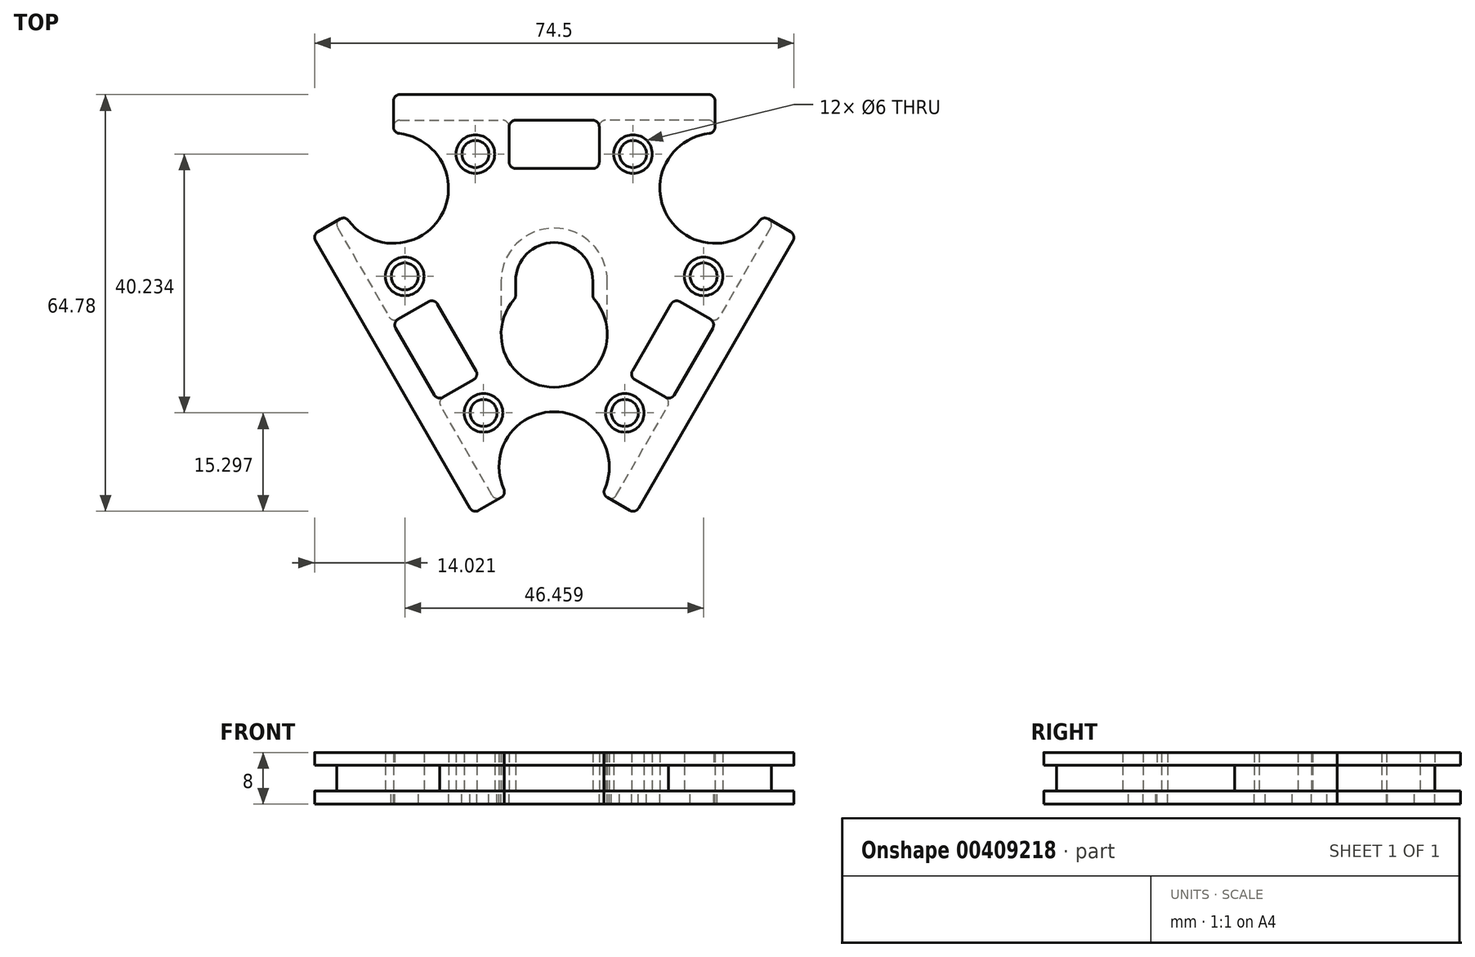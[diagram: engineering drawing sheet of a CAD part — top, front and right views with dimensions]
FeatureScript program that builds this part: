
annotation { "Feature Type Name" : "Feature", "Feature Type Description" : "" }
export const myFeature = defineFeature(function(context is Context, id is Id, definition is map)
    precondition{}
    {
        {
            var Q0;
            Q0=qCreatedBy(makeId("Top.planeOp"),FACE);
            var sketch = newSketch(context, id + "F0", { "sketchPlane" : qUnion([Q0])});
            skLineSegment(sketch, "E0.MirrorCS", {"start": v(-24, 25) * mm, "end": v(-8, 25) * mm});
            skLineSegment(sketch, "E1.MirrorCS", {"start": v(-25, 24) * mm, "end": v(-25, 23.95) * mm});
            skLineSegment(sketch, "E2.1.19", {"start": v(0, 0) * mm, "end": v(-17.58, 10.15) * mm, "construction": true});
            skArc(sketch, "E3", {"start": v(-17.58, 10.15) * mm, "mid": v(-17.37, 18.32) * mm, "end": v(-24.1, 22.95) * mm});
            skLineSegment(sketch, "E4", {"start": v(-25, 23) * mm, "end": v(0, 23) * mm, "construction": true});
            skLineSegment(sketch, "E5.top", {"start": v(0, 17.5) * mm, "end": v(-6, 17.5) * mm});
            skLineSegment(sketch, "E5.right", {"start": v(-7, 24) * mm, "end": v(-7, 18.5) * mm});
            skArc(sketch, "E6", {"start": v(6, 0) * mm, "mid": v(0, 6) * mm, "end": v(-6, 0) * mm});
            skArc(sketch, "E7", {"start": v(-6.24, -2.86) * mm, "mid": v(0, -16.5) * mm, "end": v(6.24, -2.86) * mm});
            skLineSegment(sketch, "E8", {"start": v(0, 27) * mm, "end": v(-25, 27) * mm, "construction": true});
            skCircle(sketch, "E9", {"center": v(-25, 27) * mm, "radius": 2 * mm, "construction": true});
            skLineSegment(sketch, "E10", {"start": v(-17.58, 10.15) * mm, "end": v(-7.85, 27) * mm, "construction": true});
            skLineSegment(sketch, "E11", {"start": v(-6, 0) * mm, "end": v(-6, -2.2) * mm});
            skLineSegment(sketch, "E12", {"start": v(6, -2.2) * mm, "end": v(6, 0) * mm});
            skCircle(sketch, "E13", {"center": v(-12.25, 19.75) * mm, "radius": 3 * mm});
            skCircle(sketch, "E14", {"center": v(-12.25, 19.75) * mm, "radius": 5.25 * mm, "construction": true});
            skPoint(sketch, "E15.visualSharp", {"position": v(-7, 25) * mm});
            skArc(sketch, "E15.filletArc", {"start": v(-7, 24) * mm, "mid": v(-7.3, 24.7) * mm, "end": v(-8, 25) * mm});
            skPoint(sketch, "E16.visualSharp", {"position": v(-25, 25) * mm});
            skArc(sketch, "E16.filletArc", {"start": v(-24, 25) * mm, "mid": v(-24.7, 24.7) * mm, "end": v(-25, 24) * mm});
            skPoint(sketch, "E17.visualSharp", {"position": v(-25, 23) * mm});
            skArc(sketch, "E17.filletArc", {"start": v(-25, 23.95) * mm, "mid": v(-24.74, 23.28) * mm, "end": v(-24.1, 22.95) * mm});
            skPoint(sketch, "E18.visualSharp", {"position": v(-7, 17.5) * mm});
            skArc(sketch, "E18.filletArc", {"start": v(-7, 18.5) * mm, "mid": v(-6.7, 17.8) * mm, "end": v(-6, 17.5) * mm});
            skPoint(sketch, "E19.visualSharp", {"position": v(-6, -2.59) * mm});
            skArc(sketch, "E19.filletArc", {"start": v(-6.24, -2.86) * mm, "mid": v(-6.06, -2.55) * mm, "end": v(-6, -2.2) * mm});
            skPoint(sketch, "E20.visualSharp", {"position": v(6, -2.59) * mm});
            skArc(sketch, "E20.filletArc", {"start": v(6, -2.2) * mm, "mid": v(6.06, -2.55) * mm, "end": v(6.24, -2.86) * mm});
            skLineSegment(sketch, "E21", {"start": v(0, 27) * mm, "end": v(0, 0) * mm, "construction": true});
            skLineSegment(sketch, "E22.MirrorCS", {"start": v(25, 24) * mm, "end": v(25, 23.95) * mm});
            skArc(sketch, "E23.MirrorCS", {"start": v(7, 24) * mm, "mid": v(7.3, 24.7) * mm, "end": v(8, 25) * mm});
            skArc(sketch, "E24.MirrorCS", {"start": v(24, 25) * mm, "mid": v(24.7, 24.7) * mm, "end": v(25, 24) * mm});
            skArc(sketch, "E25.MirrorCS", {"start": v(25, 23.95) * mm, "mid": v(24.74, 23.28) * mm, "end": v(24.1, 22.95) * mm});
            skArc(sketch, "E26.MirrorCS", {"start": v(7, 18.5) * mm, "mid": v(6.7, 17.8) * mm, "end": v(6, 17.5) * mm});
            skLineSegment(sketch, "E27.MirrorCS", {"start": v(25, 23) * mm, "end": v(0, 23) * mm, "construction": true});
            skLineSegment(sketch, "E28.MirrorCS", {"start": v(7, 24) * mm, "end": v(7, 18.5) * mm});
            skArc(sketch, "E29.MirrorCS", {"start": v(17.58, 10.15) * mm, "mid": v(17.37, 18.32) * mm, "end": v(24.1, 22.95) * mm});
            skPoint(sketch, "E30.MirrorP", {"position": v(25, 23) * mm});
            skPoint(sketch, "E31.MirrorP", {"position": v(25, 25) * mm});
            skPoint(sketch, "E32.MirrorP", {"position": v(7, 17.5) * mm});
            skCircle(sketch, "E33.MirrorC", {"center": v(12.25, 19.75) * mm, "radius": 5.25 * mm, "construction": true});
            skLineSegment(sketch, "E34.MirrorCS", {"start": v(24, 25) * mm, "end": v(8, 25) * mm});
            skLineSegment(sketch, "E35.MirrorCS", {"start": v(17.58, 10.15) * mm, "end": v(7.85, 27) * mm, "construction": true});
            skPoint(sketch, "E36.MirrorP", {"position": v(7, 25) * mm});
            skCircle(sketch, "E37.MirrorC", {"center": v(12.25, 19.75) * mm, "radius": 3 * mm});
            skLineSegment(sketch, "E38.MirrorCS", {"start": v(0, 17.5) * mm, "end": v(6, 17.5) * mm});
            skLineSegment(sketch, "E39.1.1", {"start": v(-15.16, -8.75) * mm, "end": v(-18.16, -3.55) * mm});
            skLineSegment(sketch, "E39.1.2", {"start": v(-33.65, 8.28) * mm, "end": v(-25.65, -5.57) * mm});
            skLineSegment(sketch, "E39.1.3", {"start": v(-15.16, -8.75) * mm, "end": v(-12.16, -13.95) * mm});
            skPoint(sketch, "E39.1.4", {"position": v(-32.42, 10.15) * mm});
            skArc(sketch, "E39.1.5", {"start": v(0, -20.3) * mm, "mid": v(-7.18, -24.2) * mm, "end": v(-7.83, -32.35) * mm});
            skPoint(sketch, "E39.1.6", {"position": v(-9.15, -34.15) * mm});
            skPoint(sketch, "E39.1.7", {"position": v(-18.66, -2.69) * mm});
            skLineSegment(sketch, "E39.1.8", {"start": v(-24.28, -5.94) * mm, "end": v(-19.52, -3.19) * mm});
            skLineSegment(sketch, "E39.1.9", {"start": v(-17.28, -18.06) * mm, "end": v(-12.52, -15.31) * mm});
            skPoint(sketch, "E39.1.10", {"position": v(-7.42, -33.15) * mm});
            skPoint(sketch, "E39.1.12", {"position": v(-34.15, 9.15) * mm});
            skArc(sketch, "E39.1.13", {"start": v(-17.58, 10.15) * mm, "mid": v(-24.55, 5.88) * mm, "end": v(-31.93, 9.4) * mm});
            skCircle(sketch, "E39.1.14", {"center": v(-10.98, -20.48) * mm, "radius": 3 * mm});
            skLineSegment(sketch, "E39.1.15", {"start": v(-9.65, -33.28) * mm, "end": v(-17.65, -19.43) * mm});
            skPoint(sketch, "E39.1.16", {"position": v(-25.15, -6.44) * mm});
            skCircle(sketch, "E39.1.17", {"center": v(-23.23, 0.73) * mm, "radius": 5.25 * mm, "construction": true});
            skPoint(sketch, "E39.1.18", {"position": v(-11.66, -14.81) * mm});
            skPoint(sketch, "E39.1.19", {"position": v(-18.15, -18.56) * mm});
            skCircle(sketch, "E39.1.20", {"center": v(-10.98, -20.48) * mm, "radius": 5.25 * mm, "construction": true});
            skCircle(sketch, "E39.1.21", {"center": v(-23.23, 0.73) * mm, "radius": 3 * mm});
            skArc(sketch, "E39.1.22", {"start": v(-17.28, -18.06) * mm, "mid": v(-17.75, -18.67) * mm, "end": v(-17.65, -19.43) * mm});
            skArc(sketch, "E39.1.23", {"start": v(-24.28, -5.94) * mm, "mid": v(-25.04, -6.04) * mm, "end": v(-25.65, -5.57) * mm});
            skArc(sketch, "E39.1.24", {"start": v(-19.52, -3.19) * mm, "mid": v(-18.76, -3.09) * mm, "end": v(-18.16, -3.55) * mm});
            skArc(sketch, "E39.1.25", {"start": v(-12.52, -15.31) * mm, "mid": v(-12.06, -14.7) * mm, "end": v(-12.16, -13.95) * mm});
            skArc(sketch, "E39.1.26", {"start": v(-33.24, 9.68) * mm, "mid": v(-32.53, 9.79) * mm, "end": v(-31.93, 9.4) * mm});
            skArc(sketch, "E39.1.27", {"start": v(-33.65, 8.28) * mm, "mid": v(-33.75, 9.04) * mm, "end": v(-33.28, 9.65) * mm});
            skArc(sketch, "E39.1.28", {"start": v(-8.24, -33.62) * mm, "mid": v(-7.79, -33.07) * mm, "end": v(-7.83, -32.35) * mm});
            skArc(sketch, "E39.1.29", {"start": v(-9.65, -33.28) * mm, "mid": v(-9.04, -33.75) * mm, "end": v(-8.28, -33.65) * mm});
            skLineSegment(sketch, "E39.1.30", {"start": v(-8.28, -33.65) * mm, "end": v(-8.24, -33.62) * mm});
            skLineSegment(sketch, "E39.1.31", {"start": v(-33.28, 9.65) * mm, "end": v(-33.24, 9.68) * mm});
            skLineSegment(sketch, "E39.2.1", {"start": v(15.16, -8.75) * mm, "end": v(12.16, -13.95) * mm});
            skLineSegment(sketch, "E39.2.2", {"start": v(9.65, -33.28) * mm, "end": v(17.65, -19.43) * mm});
            skLineSegment(sketch, "E39.2.3", {"start": v(15.16, -8.75) * mm, "end": v(18.16, -3.55) * mm});
            skPoint(sketch, "E39.2.4", {"position": v(7.42, -33.15) * mm});
            skArc(sketch, "E39.2.5", {"start": v(17.58, 10.15) * mm, "mid": v(24.55, 5.88) * mm, "end": v(31.93, 9.4) * mm});
            skPoint(sketch, "E39.2.6", {"position": v(34.15, 9.15) * mm});
            skPoint(sketch, "E39.2.7", {"position": v(11.66, -14.81) * mm});
            skLineSegment(sketch, "E39.2.8", {"start": v(17.28, -18.06) * mm, "end": v(12.52, -15.31) * mm});
            skLineSegment(sketch, "E39.2.9", {"start": v(24.28, -5.94) * mm, "end": v(19.52, -3.19) * mm});
            skPoint(sketch, "E39.2.10", {"position": v(32.42, 10.15) * mm});
            skPoint(sketch, "E39.2.12", {"position": v(9.15, -34.15) * mm});
            skArc(sketch, "E39.2.13", {"start": v(0, -20.3) * mm, "mid": v(7.18, -24.2) * mm, "end": v(7.83, -32.35) * mm});
            skCircle(sketch, "E39.2.14", {"center": v(23.23, 0.73) * mm, "radius": 3 * mm});
            skLineSegment(sketch, "E39.2.15", {"start": v(33.65, 8.28) * mm, "end": v(25.65, -5.57) * mm});
            skPoint(sketch, "E39.2.16", {"position": v(18.15, -18.56) * mm});
            skCircle(sketch, "E39.2.17", {"center": v(10.98, -20.48) * mm, "radius": 5.25 * mm, "construction": true});
            skPoint(sketch, "E39.2.18", {"position": v(18.66, -2.69) * mm});
            skPoint(sketch, "E39.2.19", {"position": v(25.15, -6.44) * mm});
            skCircle(sketch, "E39.2.20", {"center": v(23.23, 0.73) * mm, "radius": 5.25 * mm, "construction": true});
            skCircle(sketch, "E39.2.21", {"center": v(10.98, -20.48) * mm, "radius": 3 * mm});
            skArc(sketch, "E39.2.22", {"start": v(24.28, -5.94) * mm, "mid": v(25.04, -6.04) * mm, "end": v(25.65, -5.57) * mm});
            skArc(sketch, "E39.2.23", {"start": v(17.28, -18.06) * mm, "mid": v(17.75, -18.67) * mm, "end": v(17.65, -19.43) * mm});
            skArc(sketch, "E39.2.24", {"start": v(12.52, -15.31) * mm, "mid": v(12.06, -14.7) * mm, "end": v(12.16, -13.95) * mm});
            skArc(sketch, "E39.2.25", {"start": v(19.52, -3.19) * mm, "mid": v(18.76, -3.09) * mm, "end": v(18.16, -3.55) * mm});
            skArc(sketch, "E39.2.26", {"start": v(8.24, -33.62) * mm, "mid": v(7.79, -33.07) * mm, "end": v(7.83, -32.35) * mm});
            skArc(sketch, "E39.2.27", {"start": v(9.65, -33.28) * mm, "mid": v(9.04, -33.75) * mm, "end": v(8.28, -33.65) * mm});
            skArc(sketch, "E39.2.28", {"start": v(33.24, 9.68) * mm, "mid": v(32.53, 9.79) * mm, "end": v(31.93, 9.4) * mm});
            skArc(sketch, "E39.2.29", {"start": v(33.65, 8.28) * mm, "mid": v(33.75, 9.04) * mm, "end": v(33.28, 9.65) * mm});
            skLineSegment(sketch, "E39.2.30", {"start": v(33.28, 9.65) * mm, "end": v(33.24, 9.68) * mm});
            skLineSegment(sketch, "E39.2.31", {"start": v(8.28, -33.65) * mm, "end": v(8.24, -33.62) * mm});
            skSolve(sketch);
        }
        {
            var Q0;
            Q0 = qSketchRegion(id + "F0", true);
            extrude(context, id + "F1", {"entities" : qUnion([Q0]), "depth" : 4 * mm, "offsetDistance" : 25 * mm});
        }
        {
            var Q0;
            Q0=makeQuery(id+"F1.opExtrude","CAP_FACE",FACE,{"disambiguationData":[OSD([sQuery(id+"F0.wireOp",EDGE,"E0.MirrorCS"),sQuery(id+"F0.wireOp",EDGE,"E1.MirrorCS"),sQuery(id+"F0.wireOp",EDGE,"E3"),sQuery(id+"F0.wireOp",EDGE,"E5.top"),sQuery(id+"F0.wireOp",EDGE,"E5.right"),sQuery(id+"F0.wireOp",EDGE,"E6"),sQuery(id+"F0.wireOp",EDGE,"E7"),sQuery(id+"F0.wireOp",EDGE,"E11"),sQuery(id+"F0.wireOp",EDGE,"E12"),sQuery(id+"F0.wireOp",EDGE,"E13"),sQuery(id+"F0.wireOp",EDGE,"E15.filletArc"),sQuery(id+"F0.wireOp",EDGE,"E16.filletArc"),sQuery(id+"F0.wireOp",EDGE,"E17.filletArc"),sQuery(id+"F0.wireOp",EDGE,"E18.filletArc"),sQuery(id+"F0.wireOp",EDGE,"E19.filletArc"),sQuery(id+"F0.wireOp",EDGE,"E20.filletArc"),sQuery(id+"F0.wireOp",EDGE,"E22.MirrorCS"),sQuery(id+"F0.wireOp",EDGE,"E23.MirrorCS"),sQuery(id+"F0.wireOp",EDGE,"E24.MirrorCS"),sQuery(id+"F0.wireOp",EDGE,"E25.MirrorCS"),sQuery(id+"F0.wireOp",EDGE,"E26.MirrorCS"),sQuery(id+"F0.wireOp",EDGE,"E28.MirrorCS"),sQuery(id+"F0.wireOp",EDGE,"E29.MirrorCS"),sQuery(id+"F0.wireOp",EDGE,"E34.MirrorCS"),sQuery(id+"F0.wireOp",EDGE,"E37.MirrorC"),sQuery(id+"F0.wireOp",EDGE,"E38.MirrorCS"),sQuery(id+"F0.wireOp",EDGE,"E39.1.1"),sQuery(id+"F0.wireOp",EDGE,"E39.1.2"),sQuery(id+"F0.wireOp",EDGE,"E39.1.3"),sQuery(id+"F0.wireOp",EDGE,"E39.1.5"),sQuery(id+"F0.wireOp",EDGE,"E39.1.8"),sQuery(id+"F0.wireOp",EDGE,"E39.1.9"),sQuery(id+"F0.wireOp",EDGE,"E39.1.13"),sQuery(id+"F0.wireOp",EDGE,"E39.1.14"),sQuery(id+"F0.wireOp",EDGE,"E39.1.15"),sQuery(id+"F0.wireOp",EDGE,"E39.1.21"),sQuery(id+"F0.wireOp",EDGE,"E39.1.22"),sQuery(id+"F0.wireOp",EDGE,"E39.1.23"),sQuery(id+"F0.wireOp",EDGE,"E39.1.24"),sQuery(id+"F0.wireOp",EDGE,"E39.1.25"),sQuery(id+"F0.wireOp",EDGE,"E39.1.26"),sQuery(id+"F0.wireOp",EDGE,"E39.1.27"),sQuery(id+"F0.wireOp",EDGE,"E39.1.28"),sQuery(id+"F0.wireOp",EDGE,"E39.1.29"),sQuery(id+"F0.wireOp",EDGE,"E39.1.30"),sQuery(id+"F0.wireOp",EDGE,"E39.1.31"),sQuery(id+"F0.wireOp",EDGE,"E39.2.1"),sQuery(id+"F0.wireOp",EDGE,"E39.2.2"),sQuery(id+"F0.wireOp",EDGE,"E39.2.3"),sQuery(id+"F0.wireOp",EDGE,"E39.2.5"),sQuery(id+"F0.wireOp",EDGE,"E39.2.8"),sQuery(id+"F0.wireOp",EDGE,"E39.2.9"),sQuery(id+"F0.wireOp",EDGE,"E39.2.13"),sQuery(id+"F0.wireOp",EDGE,"E39.2.14"),sQuery(id+"F0.wireOp",EDGE,"E39.2.15"),sQuery(id+"F0.wireOp",EDGE,"E39.2.21"),sQuery(id+"F0.wireOp",EDGE,"E39.2.22"),sQuery(id+"F0.wireOp",EDGE,"E39.2.23"),sQuery(id+"F0.wireOp",EDGE,"E39.2.24"),sQuery(id+"F0.wireOp",EDGE,"E39.2.25"),sQuery(id+"F0.wireOp",EDGE,"E39.2.26"),sQuery(id+"F0.wireOp",EDGE,"E39.2.27"),sQuery(id+"F0.wireOp",EDGE,"E39.2.28"),sQuery(id+"F0.wireOp",EDGE,"E39.2.29"),sQuery(id+"F0.wireOp",EDGE,"E39.2.30"),sQuery(id+"F0.wireOp",EDGE,"E39.2.31")])],"isStart":false});
            var sketch = newSketch(context, id + "F2", { "sketchPlane" : qUnion([Q0])});
            skLineSegment(sketch, "E40.1.19", {"start": v(0, 0) * mm, "end": v(-17.58, 10.15) * mm, "construction": true});
            skArc(sketch, "E41", {"start": v(-17.58, 10.15) * mm, "mid": v(-17.37, 18.32) * mm, "end": v(-24.1, 22.95) * mm});
            skLineSegment(sketch, "E42", {"start": v(-25, 23) * mm, "end": v(0, 23) * mm, "construction": true});
            skArc(sketch, "E43", {"start": v(6, 0) * mm, "mid": v(0, 6) * mm, "end": v(-6, 0) * mm});
            skArc(sketch, "E44", {"start": v(-6.24, -2.86) * mm, "mid": v(0, -16.5) * mm, "end": v(6.24, -2.86) * mm});
            skLineSegment(sketch, "E45", {"start": v(0, 27) * mm, "end": v(-25, 27) * mm, "construction": true});
            skCircle(sketch, "E46", {"center": v(-25, 27) * mm, "radius": 2 * mm, "construction": true});
            skLineSegment(sketch, "E47", {"start": v(-17.58, 10.15) * mm, "end": v(-7.85, 27) * mm, "construction": true});
            skLineSegment(sketch, "E48", {"start": v(-6, 0) * mm, "end": v(-6, -2.2) * mm});
            skLineSegment(sketch, "E49", {"start": v(6, -2.2) * mm, "end": v(6, 0) * mm});
            skCircle(sketch, "E50", {"center": v(-12.25, 19.75) * mm, "radius": 2.1 * mm});
            skCircle(sketch, "E51", {"center": v(-12.25, 19.75) * mm, "radius": 5.25 * mm, "construction": true});
            skPoint(sketch, "E52.visualSharp", {"position": v(-25, 25) * mm});
            skPoint(sketch, "E53.visualSharp", {"position": v(-25, 23) * mm});
            skArc(sketch, "E53.filletArc", {"start": v(-25, 23.95) * mm, "mid": v(-24.74, 23.28) * mm, "end": v(-24.1, 22.95) * mm});
            skPoint(sketch, "E54.visualSharp", {"position": v(-6, -2.59) * mm});
            skArc(sketch, "E54.filletArc", {"start": v(-6.24, -2.86) * mm, "mid": v(-6.06, -2.55) * mm, "end": v(-6, -2.2) * mm});
            skPoint(sketch, "E55.visualSharp", {"position": v(6, -2.59) * mm});
            skArc(sketch, "E55.filletArc", {"start": v(6, -2.2) * mm, "mid": v(6.06, -2.55) * mm, "end": v(6.24, -2.86) * mm});
            skLineSegment(sketch, "E56", {"start": v(0, 27) * mm, "end": v(0, 0) * mm, "construction": true});
            skLineSegment(sketch, "E57", {"start": v(0, 29) * mm, "end": v(-24, 29) * mm});
            skLineSegment(sketch, "E58", {"start": v(-25, 28) * mm, "end": v(-25, 23.95) * mm});
            skPoint(sketch, "E59.visualSharp", {"position": v(-25, 29) * mm});
            skArc(sketch, "E59.filletArc", {"start": v(-24, 29) * mm, "mid": v(-24.7, 28.7) * mm, "end": v(-25, 28) * mm});
            skLineSegment(sketch, "E60", {"start": v(-25, 25) * mm, "end": v(0, 25) * mm, "construction": true});
            skLineSegment(sketch, "E61", {"start": v(0, 25) * mm, "end": v(-6, 25) * mm});
            skLineSegment(sketch, "E62", {"start": v(-7, 24) * mm, "end": v(-7, 18.5) * mm});
            skLineSegment(sketch, "E63", {"start": v(-6, 17.5) * mm, "end": v(0, 17.5) * mm});
            skPoint(sketch, "E64.visualSharp", {"position": v(-7, 17.5) * mm});
            skArc(sketch, "E64.filletArc", {"start": v(-7, 18.5) * mm, "mid": v(-6.7, 17.8) * mm, "end": v(-6, 17.5) * mm});
            skPoint(sketch, "E65.visualSharp", {"position": v(-7, 25) * mm});
            skArc(sketch, "E65.filletArc", {"start": v(-6, 25) * mm, "mid": v(-6.7, 24.7) * mm, "end": v(-7, 24) * mm});
            skArc(sketch, "E66.MirrorCS", {"start": v(25, 23.95) * mm, "mid": v(24.74, 23.28) * mm, "end": v(24.1, 22.95) * mm});
            skArc(sketch, "E67.MirrorCS", {"start": v(6, 25) * mm, "mid": v(6.7, 24.7) * mm, "end": v(7, 24) * mm});
            skArc(sketch, "E68.MirrorCS", {"start": v(7, 18.5) * mm, "mid": v(6.7, 17.8) * mm, "end": v(6, 17.5) * mm});
            skArc(sketch, "E69.MirrorCS", {"start": v(24, 29) * mm, "mid": v(24.7, 28.7) * mm, "end": v(25, 28) * mm});
            skLineSegment(sketch, "E70.MirrorCS", {"start": v(0, 25) * mm, "end": v(6, 25) * mm});
            skPoint(sketch, "E71.MirrorP", {"position": v(25, 29) * mm});
            skPoint(sketch, "E72.MirrorP", {"position": v(25, 23) * mm});
            skCircle(sketch, "E73.MirrorC", {"center": v(12.25, 19.75) * mm, "radius": 2.1 * mm});
            skLineSegment(sketch, "E74.MirrorCS", {"start": v(6, 17.5) * mm, "end": v(0, 17.5) * mm});
            skLineSegment(sketch, "E75.MirrorCS", {"start": v(0, 29) * mm, "end": v(24, 29) * mm});
            skPoint(sketch, "E76.MirrorP", {"position": v(25, 25) * mm});
            skPoint(sketch, "E77.MirrorP", {"position": v(7, 25) * mm});
            skArc(sketch, "E78.MirrorCS", {"start": v(17.58, 10.15) * mm, "mid": v(17.37, 18.32) * mm, "end": v(24.1, 22.95) * mm});
            skCircle(sketch, "E79.MirrorC", {"center": v(25, 27) * mm, "radius": 2 * mm, "construction": true});
            skLineSegment(sketch, "E80.MirrorCS", {"start": v(17.58, 10.15) * mm, "end": v(7.85, 27) * mm, "construction": true});
            skPoint(sketch, "E81.MirrorP", {"position": v(7, 17.5) * mm});
            skLineSegment(sketch, "E82.MirrorCS", {"start": v(25, 25) * mm, "end": v(0, 25) * mm, "construction": true});
            skLineSegment(sketch, "E83.MirrorCS", {"start": v(25, 23) * mm, "end": v(0, 23) * mm, "construction": true});
            skLineSegment(sketch, "E84.MirrorCS", {"start": v(0, 27) * mm, "end": v(25, 27) * mm, "construction": true});
            skLineSegment(sketch, "E85.MirrorCS", {"start": v(25, 28) * mm, "end": v(25, 23.95) * mm});
            skLineSegment(sketch, "E86.MirrorCS", {"start": v(7, 24) * mm, "end": v(7, 18.5) * mm});
            skCircle(sketch, "E87.MirrorC", {"center": v(12.25, 19.75) * mm, "radius": 5.25 * mm, "construction": true});
            skLineSegment(sketch, "E88.1.0", {"start": v(-25.11, -14.5) * mm, "end": v(-13.11, -35.28) * mm});
            skLineSegment(sketch, "E88.1.1", {"start": v(-12.16, -13.95) * mm, "end": v(-15.16, -8.75) * mm});
            skLineSegment(sketch, "E88.1.2", {"start": v(-9.15, -34.15) * mm, "end": v(-21.65, -12.5) * mm, "construction": true});
            skPoint(sketch, "E88.1.3", {"position": v(-12.61, -36.15) * mm});
            skPoint(sketch, "E88.1.4", {"position": v(-9.15, -34.15) * mm});
            skLineSegment(sketch, "E88.1.5", {"start": v(-23.38, -13.5) * mm, "end": v(-35.88, 8.15) * mm, "construction": true});
            skPoint(sketch, "E88.1.6", {"position": v(-34.15, 9.15) * mm});
            skLineSegment(sketch, "E88.1.7", {"start": v(-24.28, -5.94) * mm, "end": v(-19.52, -3.19) * mm});
            skCircle(sketch, "E88.1.8", {"center": v(-10.88, -35.15) * mm, "radius": 2 * mm, "construction": true});
            skArc(sketch, "E88.1.9", {"start": v(0, -20.3) * mm, "mid": v(-7.18, -24.2) * mm, "end": v(-7.83, -32.35) * mm});
            skLineSegment(sketch, "E88.1.10", {"start": v(-23.38, -13.5) * mm, "end": v(-10.88, -35.15) * mm, "construction": true});
            skPoint(sketch, "E88.1.11", {"position": v(-25.15, -6.44) * mm});
            skPoint(sketch, "E88.1.12", {"position": v(-7.42, -33.15) * mm});
            skPoint(sketch, "E88.1.13", {"position": v(-18.66, -2.69) * mm});
            skPoint(sketch, "E88.1.14", {"position": v(-37.61, 7.15) * mm});
            skLineSegment(sketch, "E88.1.15", {"start": v(-32.42, 10.15) * mm, "end": v(-19.92, -11.5) * mm, "construction": true});
            skCircle(sketch, "E88.1.16", {"center": v(-10.98, -20.48) * mm, "radius": 5.25 * mm, "construction": true});
            skCircle(sketch, "E88.1.17", {"center": v(-35.88, 8.15) * mm, "radius": 2 * mm, "construction": true});
            skCircle(sketch, "E88.1.18", {"center": v(-23.23, 0.73) * mm, "radius": 2.1 * mm});
            skPoint(sketch, "E88.1.19", {"position": v(-18.15, -18.56) * mm});
            skLineSegment(sketch, "E88.1.20", {"start": v(-17.58, 10.15) * mm, "end": v(-27.3, -6.7) * mm, "construction": true});
            skLineSegment(sketch, "E88.1.21", {"start": v(0, -20.3) * mm, "end": v(-19.46, -20.3) * mm, "construction": true});
            skLineSegment(sketch, "E88.1.22", {"start": v(-18.16, -3.55) * mm, "end": v(-15.16, -8.75) * mm});
            skPoint(sketch, "E88.1.23", {"position": v(-11.66, -14.81) * mm});
            skArc(sketch, "E88.1.24", {"start": v(-17.58, 10.15) * mm, "mid": v(-24.55, 5.88) * mm, "end": v(-31.93, 9.4) * mm});
            skLineSegment(sketch, "E88.1.25", {"start": v(-25.11, -14.5) * mm, "end": v(-37.11, 6.28) * mm});
            skPoint(sketch, "E88.1.26", {"position": v(-32.42, 10.15) * mm});
            skLineSegment(sketch, "E88.1.27", {"start": v(-34.15, 9.15) * mm, "end": v(-21.65, -12.5) * mm, "construction": true});
            skCircle(sketch, "E88.1.28", {"center": v(-23.23, 0.73) * mm, "radius": 5.25 * mm, "construction": true});
            skCircle(sketch, "E88.1.29", {"center": v(-10.98, -20.48) * mm, "radius": 2.1 * mm});
            skLineSegment(sketch, "E88.1.30", {"start": v(-7.42, -33.15) * mm, "end": v(-19.92, -11.5) * mm, "construction": true});
            skLineSegment(sketch, "E88.1.31", {"start": v(-21.65, -12.5) * mm, "end": v(-18.65, -17.7) * mm});
            skLineSegment(sketch, "E88.1.32", {"start": v(-21.65, -12.5) * mm, "end": v(-24.65, -7.3) * mm});
            skLineSegment(sketch, "E88.1.33", {"start": v(-17.28, -18.06) * mm, "end": v(-12.52, -15.31) * mm});
            skArc(sketch, "E88.1.34", {"start": v(-8.24, -33.62) * mm, "mid": v(-7.79, -33.07) * mm, "end": v(-7.83, -32.35) * mm});
            skArc(sketch, "E88.1.35", {"start": v(-19.52, -3.19) * mm, "mid": v(-18.76, -3.09) * mm, "end": v(-18.16, -3.55) * mm});
            skArc(sketch, "E88.1.36", {"start": v(-24.65, -7.3) * mm, "mid": v(-24.75, -6.55) * mm, "end": v(-24.28, -5.94) * mm});
            skArc(sketch, "E88.1.37", {"start": v(-33.24, 9.68) * mm, "mid": v(-32.53, 9.79) * mm, "end": v(-31.93, 9.4) * mm});
            skArc(sketch, "E88.1.38", {"start": v(-18.65, -17.7) * mm, "mid": v(-18.04, -18.16) * mm, "end": v(-17.28, -18.06) * mm});
            skArc(sketch, "E88.1.39", {"start": v(-13.11, -35.28) * mm, "mid": v(-12.5, -35.75) * mm, "end": v(-11.75, -35.65) * mm});
            skLineSegment(sketch, "E88.1.40", {"start": v(-11.75, -35.65) * mm, "end": v(-8.24, -33.62) * mm});
            skLineSegment(sketch, "E88.1.41", {"start": v(-36.75, 7.65) * mm, "end": v(-33.24, 9.68) * mm});
            skArc(sketch, "E88.1.42", {"start": v(-37.11, 6.28) * mm, "mid": v(-37.21, 7.04) * mm, "end": v(-36.75, 7.65) * mm});
            skArc(sketch, "E88.1.43", {"start": v(-12.52, -15.31) * mm, "mid": v(-12.06, -14.7) * mm, "end": v(-12.16, -13.95) * mm});
            skLineSegment(sketch, "E88.2.0", {"start": v(25.11, -14.5) * mm, "end": v(37.11, 6.28) * mm});
            skLineSegment(sketch, "E88.2.1", {"start": v(18.16, -3.55) * mm, "end": v(15.16, -8.75) * mm});
            skLineSegment(sketch, "E88.2.2", {"start": v(34.15, 9.15) * mm, "end": v(21.65, -12.5) * mm, "construction": true});
            skPoint(sketch, "E88.2.3", {"position": v(37.61, 7.15) * mm});
            skPoint(sketch, "E88.2.4", {"position": v(34.15, 9.15) * mm});
            skLineSegment(sketch, "E88.2.5", {"start": v(23.38, -13.5) * mm, "end": v(10.88, -35.15) * mm, "construction": true});
            skPoint(sketch, "E88.2.6", {"position": v(9.15, -34.15) * mm});
            skLineSegment(sketch, "E88.2.7", {"start": v(17.28, -18.06) * mm, "end": v(12.52, -15.31) * mm});
            skCircle(sketch, "E88.2.8", {"center": v(35.88, 8.15) * mm, "radius": 2 * mm, "construction": true});
            skArc(sketch, "E88.2.9", {"start": v(17.58, 10.15) * mm, "mid": v(24.55, 5.88) * mm, "end": v(31.93, 9.4) * mm});
            skLineSegment(sketch, "E88.2.10", {"start": v(23.38, -13.5) * mm, "end": v(35.88, 8.15) * mm, "construction": true});
            skPoint(sketch, "E88.2.11", {"position": v(18.15, -18.56) * mm});
            skPoint(sketch, "E88.2.12", {"position": v(32.42, 10.15) * mm});
            skPoint(sketch, "E88.2.13", {"position": v(11.66, -14.81) * mm});
            skPoint(sketch, "E88.2.14", {"position": v(12.61, -36.15) * mm});
            skLineSegment(sketch, "E88.2.15", {"start": v(7.42, -33.15) * mm, "end": v(19.92, -11.5) * mm, "construction": true});
            skCircle(sketch, "E88.2.16", {"center": v(23.23, 0.73) * mm, "radius": 5.25 * mm, "construction": true});
            skCircle(sketch, "E88.2.17", {"center": v(10.88, -35.15) * mm, "radius": 2 * mm, "construction": true});
            skCircle(sketch, "E88.2.18", {"center": v(10.98, -20.48) * mm, "radius": 2.1 * mm});
            skPoint(sketch, "E88.2.19", {"position": v(25.15, -6.44) * mm});
            skLineSegment(sketch, "E88.2.20", {"start": v(0, -20.3) * mm, "end": v(19.46, -20.3) * mm, "construction": true});
            skLineSegment(sketch, "E88.2.21", {"start": v(17.58, 10.15) * mm, "end": v(27.3, -6.7) * mm, "construction": true});
            skLineSegment(sketch, "E88.2.22", {"start": v(12.16, -13.95) * mm, "end": v(15.16, -8.75) * mm});
            skPoint(sketch, "E88.2.23", {"position": v(18.66, -2.69) * mm});
            skArc(sketch, "E88.2.24", {"start": v(0, -20.3) * mm, "mid": v(7.18, -24.2) * mm, "end": v(7.83, -32.35) * mm});
            skLineSegment(sketch, "E88.2.25", {"start": v(25.11, -14.5) * mm, "end": v(13.11, -35.28) * mm});
            skPoint(sketch, "E88.2.26", {"position": v(7.42, -33.15) * mm});
            skLineSegment(sketch, "E88.2.27", {"start": v(9.15, -34.15) * mm, "end": v(21.65, -12.5) * mm, "construction": true});
            skCircle(sketch, "E88.2.28", {"center": v(10.98, -20.48) * mm, "radius": 5.25 * mm, "construction": true});
            skCircle(sketch, "E88.2.29", {"center": v(23.23, 0.73) * mm, "radius": 2.1 * mm});
            skLineSegment(sketch, "E88.2.30", {"start": v(32.42, 10.15) * mm, "end": v(19.92, -11.5) * mm, "construction": true});
            skLineSegment(sketch, "E88.2.31", {"start": v(21.65, -12.5) * mm, "end": v(24.65, -7.3) * mm});
            skLineSegment(sketch, "E88.2.32", {"start": v(21.65, -12.5) * mm, "end": v(18.65, -17.7) * mm});
            skLineSegment(sketch, "E88.2.33", {"start": v(24.28, -5.94) * mm, "end": v(19.52, -3.19) * mm});
            skArc(sketch, "E88.2.34", {"start": v(33.24, 9.68) * mm, "mid": v(32.53, 9.79) * mm, "end": v(31.93, 9.4) * mm});
            skArc(sketch, "E88.2.35", {"start": v(12.52, -15.31) * mm, "mid": v(12.06, -14.7) * mm, "end": v(12.16, -13.95) * mm});
            skArc(sketch, "E88.2.36", {"start": v(18.65, -17.7) * mm, "mid": v(18.04, -18.16) * mm, "end": v(17.28, -18.06) * mm});
            skArc(sketch, "E88.2.37", {"start": v(8.24, -33.62) * mm, "mid": v(7.79, -33.07) * mm, "end": v(7.83, -32.35) * mm});
            skArc(sketch, "E88.2.38", {"start": v(24.65, -7.3) * mm, "mid": v(24.75, -6.55) * mm, "end": v(24.28, -5.94) * mm});
            skArc(sketch, "E88.2.39", {"start": v(37.11, 6.28) * mm, "mid": v(37.21, 7.04) * mm, "end": v(36.75, 7.65) * mm});
            skLineSegment(sketch, "E88.2.40", {"start": v(36.75, 7.65) * mm, "end": v(33.24, 9.68) * mm});
            skLineSegment(sketch, "E88.2.41", {"start": v(11.75, -35.65) * mm, "end": v(8.24, -33.62) * mm});
            skArc(sketch, "E88.2.42", {"start": v(13.11, -35.28) * mm, "mid": v(12.5, -35.75) * mm, "end": v(11.75, -35.65) * mm});
            skArc(sketch, "E88.2.43", {"start": v(19.52, -3.19) * mm, "mid": v(18.76, -3.09) * mm, "end": v(18.16, -3.55) * mm});
            skSolve(sketch);
        }
        {
            var Q0;
            Q0=makeQuery(id+"F2.imprint","IMPRINT",FACE,{"disambiguationData":[TD([[makeQuery(id+"F2.imprint","IMPRINT",EDGE,{"derivedFrom":sQuery(id+"F2.wireOp",EDGE,"E43")}),-1.0]])]});
            var Q1;
            Q1=makeQuery(id+"F2.imprint","IMPRINT",FACE,{"disambiguationData":[TD([[makeQuery(id+"F2.imprint","IMPRINT",EDGE,{"derivedFrom":sQuery(id+"F2.wireOp",EDGE,"E57")}),1.0]])]});
            var Q2;
            Q2=makeQuery(id+"F2.imprint","IMPRINT",FACE,{"disambiguationData":[TD([[makeQuery(id+"F2.imprint","IMPRINT",EDGE,{"derivedFrom":sQuery(id+"F2.wireOp",EDGE,"E88.1.0")}),1.0]])]});
            var Q3;
            Q3=makeQuery(id+"F2.imprint","IMPRINT",FACE,{"disambiguationData":[TD([[makeQuery(id+"F2.imprint","IMPRINT",EDGE,{"derivedFrom":sQuery(id+"F2.wireOp",EDGE,"E88.2.0")}),1.0]])]});
            extrude(context, id + "F3", {"entities" : qUnion([Q0, Q1, Q2, Q3]), "depth" : 2 * mm, "offsetDistance" : 25 * mm});
        }
        {
            var Q0;
            Q0=qCreatedBy(makeId("Top.planeOp"),FACE);
            var sketch = newSketch(context, id + "F4", { "sketchPlane" : qUnion([Q0])});
            skLineSegment(sketch, "E89.1.19", {"start": v(0, 0) * mm, "end": v(-17.58, 10.15) * mm, "construction": true});
            skArc(sketch, "E90", {"start": v(-17.58, 10.15) * mm, "mid": v(-17.37, 18.32) * mm, "end": v(-24.1, 22.95) * mm});
            skLineSegment(sketch, "E91", {"start": v(-25, 23) * mm, "end": v(0, 23) * mm, "construction": true});
            skArc(sketch, "E92", {"start": v(8.25, 0) * mm, "mid": v(0, 8.25) * mm, "end": v(-8.25, 0) * mm});
            skArc(sketch, "E93", {"start": v(-8.25, -8.25) * mm, "mid": v(0, -16.5) * mm, "end": v(8.25, -8.25) * mm});
            skLineSegment(sketch, "E94", {"start": v(0, 27) * mm, "end": v(-25, 27) * mm, "construction": true});
            skCircle(sketch, "E95", {"center": v(-25, 27) * mm, "radius": 2 * mm, "construction": true});
            skLineSegment(sketch, "E96", {"start": v(-17.58, 10.15) * mm, "end": v(-7.85, 27) * mm, "construction": true});
            skLineSegment(sketch, "E97", {"start": v(-8.25, 0) * mm, "end": v(-8.25, -8.25) * mm});
            skLineSegment(sketch, "E98", {"start": v(8.25, -8.25) * mm, "end": v(8.25, 0) * mm});
            skCircle(sketch, "E99", {"center": v(-12.25, 19.75) * mm, "radius": 2.1 * mm});
            skCircle(sketch, "E100", {"center": v(-12.25, 19.75) * mm, "radius": 5.25 * mm, "construction": true});
            skPoint(sketch, "E101.visualSharp", {"position": v(-8.25, -8.25) * mm});
            skLineSegment(sketch, "E101.filletArc", {"start": v(-8.25, -8.25) * mm, "end": v(-8.25, -8.25) * mm});
            skPoint(sketch, "E102.visualSharp", {"position": v(8.25, -8.25) * mm});
            skLineSegment(sketch, "E102.filletArc", {"start": v(8.25, -8.25) * mm, "end": v(8.25, -8.25) * mm});
            skLineSegment(sketch, "E103", {"start": v(0, 27) * mm, "end": v(0, 0) * mm, "construction": true});
            skLineSegment(sketch, "E104", {"start": v(0, 29) * mm, "end": v(-24, 29) * mm});
            skLineSegment(sketch, "E105", {"start": v(-25, 25) * mm, "end": v(0, 25) * mm, "construction": true});
            skLineSegment(sketch, "E106", {"start": v(0, 25) * mm, "end": v(-6, 25) * mm});
            skLineSegment(sketch, "E107", {"start": v(-7, 24) * mm, "end": v(-7, 18.5) * mm});
            skLineSegment(sketch, "E108", {"start": v(-6, 17.5) * mm, "end": v(0, 17.5) * mm});
            skPoint(sketch, "E109.visualSharp", {"position": v(-7, 17.5) * mm});
            skArc(sketch, "E109.filletArc", {"start": v(-7, 18.5) * mm, "mid": v(-6.7, 17.8) * mm, "end": v(-6, 17.5) * mm});
            skPoint(sketch, "E110.visualSharp", {"position": v(-7, 25) * mm});
            skArc(sketch, "E110.filletArc", {"start": v(-6, 25) * mm, "mid": v(-6.7, 24.7) * mm, "end": v(-7, 24) * mm});
            skLineSegment(sketch, "E111", {"start": v(-25, 28) * mm, "end": v(-25, 23.95) * mm});
            skPoint(sketch, "E112.visualSharp", {"position": v(-25, 29) * mm});
            skArc(sketch, "E112.filletArc", {"start": v(-24, 29) * mm, "mid": v(-24.7, 28.7) * mm, "end": v(-25, 28) * mm});
            skPoint(sketch, "E113.visualSharp", {"position": v(-25, 23) * mm});
            skArc(sketch, "E113.filletArc", {"start": v(-25, 23.95) * mm, "mid": v(-24.74, 23.28) * mm, "end": v(-24.1, 22.95) * mm});
            skArc(sketch, "E114.MirrorCS", {"start": v(24, 29) * mm, "mid": v(24.7, 28.7) * mm, "end": v(25, 28) * mm});
            skArc(sketch, "E115.MirrorCS", {"start": v(6, 25) * mm, "mid": v(6.7, 24.7) * mm, "end": v(7, 24) * mm});
            skArc(sketch, "E116.MirrorCS", {"start": v(25, 23.95) * mm, "mid": v(24.74, 23.28) * mm, "end": v(24.1, 22.95) * mm});
            skArc(sketch, "E117.MirrorCS", {"start": v(7, 18.5) * mm, "mid": v(6.7, 17.8) * mm, "end": v(6, 17.5) * mm});
            skLineSegment(sketch, "E118.MirrorCS", {"start": v(25, 28) * mm, "end": v(25, 23.95) * mm});
            skLineSegment(sketch, "E119.MirrorCS", {"start": v(0, 25) * mm, "end": v(6, 25) * mm});
            skLineSegment(sketch, "E120.MirrorCS", {"start": v(7, 24) * mm, "end": v(7, 18.5) * mm});
            skLineSegment(sketch, "E121.MirrorCS", {"start": v(0, 27) * mm, "end": v(25, 27) * mm, "construction": true});
            skLineSegment(sketch, "E122.MirrorCS", {"start": v(25, 25) * mm, "end": v(0, 25) * mm, "construction": true});
            skLineSegment(sketch, "E123.MirrorCS", {"start": v(0, 29) * mm, "end": v(24, 29) * mm});
            skPoint(sketch, "E124.MirrorP", {"position": v(25, 23) * mm});
            skPoint(sketch, "E125.MirrorP", {"position": v(25, 29) * mm});
            skArc(sketch, "E126.MirrorCS", {"start": v(17.58, 10.15) * mm, "mid": v(17.37, 18.32) * mm, "end": v(24.1, 22.95) * mm});
            skCircle(sketch, "E127.MirrorC", {"center": v(25, 27) * mm, "radius": 2 * mm, "construction": true});
            skLineSegment(sketch, "E128.MirrorCS", {"start": v(6, 17.5) * mm, "end": v(0, 17.5) * mm});
            skCircle(sketch, "E129.MirrorC", {"center": v(12.25, 19.75) * mm, "radius": 2.1 * mm});
            skPoint(sketch, "E130.MirrorP", {"position": v(7, 17.5) * mm});
            skLineSegment(sketch, "E131.MirrorCS", {"start": v(17.58, 10.15) * mm, "end": v(7.85, 27) * mm, "construction": true});
            skLineSegment(sketch, "E132.MirrorCS", {"start": v(25, 23) * mm, "end": v(0, 23) * mm, "construction": true});
            skPoint(sketch, "E133.MirrorP", {"position": v(7, 25) * mm});
            skCircle(sketch, "E134.MirrorC", {"center": v(12.25, 19.75) * mm, "radius": 5.25 * mm, "construction": true});
            skLineSegment(sketch, "E135.1.0", {"start": v(-23.38, -13.5) * mm, "end": v(-10.88, -35.15) * mm, "construction": true});
            skLineSegment(sketch, "E135.1.1", {"start": v(-34.15, 9.15) * mm, "end": v(-21.65, -12.5) * mm, "construction": true});
            skCircle(sketch, "E135.1.2", {"center": v(-10.98, -20.48) * mm, "radius": 5.25 * mm, "construction": true});
            skCircle(sketch, "E135.1.3", {"center": v(-23.23, 0.73) * mm, "radius": 2.1 * mm});
            skPoint(sketch, "E135.1.4", {"position": v(-11.66, -14.81) * mm});
            skCircle(sketch, "E135.1.5", {"center": v(-23.23, 0.73) * mm, "radius": 5.25 * mm, "construction": true});
            skCircle(sketch, "E135.1.6", {"center": v(-10.88, -35.15) * mm, "radius": 2 * mm, "construction": true});
            skLineSegment(sketch, "E135.1.7", {"start": v(-25.11, -14.5) * mm, "end": v(-37.11, 6.28) * mm});
            skArc(sketch, "E135.1.8", {"start": v(-17.58, 10.15) * mm, "mid": v(-24.55, 5.88) * mm, "end": v(-31.93, 9.4) * mm});
            skLineSegment(sketch, "E135.1.9", {"start": v(-32.42, 10.15) * mm, "end": v(-19.92, -11.5) * mm, "construction": true});
            skArc(sketch, "E135.1.10", {"start": v(0, -20.3) * mm, "mid": v(-7.18, -24.2) * mm, "end": v(-7.83, -32.35) * mm});
            skLineSegment(sketch, "E135.1.11", {"start": v(-18.16, -3.55) * mm, "end": v(-15.16, -8.75) * mm});
            skCircle(sketch, "E135.1.12", {"center": v(-10.98, -20.48) * mm, "radius": 2.1 * mm});
            skPoint(sketch, "E135.1.13", {"position": v(-32.42, 10.15) * mm});
            skPoint(sketch, "E135.1.14", {"position": v(-25.15, -6.44) * mm});
            skLineSegment(sketch, "E135.1.15", {"start": v(-17.58, 10.15) * mm, "end": v(-27.3, -6.7) * mm, "construction": true});
            skLineSegment(sketch, "E135.1.16", {"start": v(-23.38, -13.5) * mm, "end": v(-35.88, 8.15) * mm, "construction": true});
            skCircle(sketch, "E135.1.17", {"center": v(-35.88, 8.15) * mm, "radius": 2 * mm, "construction": true});
            skPoint(sketch, "E135.1.18", {"position": v(-18.15, -18.56) * mm});
            skLineSegment(sketch, "E135.1.19", {"start": v(-7.42, -33.15) * mm, "end": v(-19.92, -11.5) * mm, "construction": true});
            skLineSegment(sketch, "E135.1.20", {"start": v(-9.15, -34.15) * mm, "end": v(-21.65, -12.5) * mm, "construction": true});
            skPoint(sketch, "E135.1.21", {"position": v(-18.66, -2.69) * mm});
            skLineSegment(sketch, "E135.1.22", {"start": v(-24.28, -5.94) * mm, "end": v(-19.52, -3.19) * mm});
            skLineSegment(sketch, "E135.1.23", {"start": v(-12.16, -13.95) * mm, "end": v(-15.16, -8.75) * mm});
            skPoint(sketch, "E135.1.24", {"position": v(-37.61, 7.15) * mm});
            skLineSegment(sketch, "E135.1.25", {"start": v(-25.11, -14.5) * mm, "end": v(-13.11, -35.28) * mm});
            skPoint(sketch, "E135.1.26", {"position": v(-12.61, -36.15) * mm});
            skLineSegment(sketch, "E135.1.27", {"start": v(0, -20.3) * mm, "end": v(-19.46, -20.3) * mm, "construction": true});
            skPoint(sketch, "E135.1.28", {"position": v(-7.42, -33.15) * mm});
            skLineSegment(sketch, "E135.1.29", {"start": v(-17.28, -18.06) * mm, "end": v(-12.52, -15.31) * mm});
            skLineSegment(sketch, "E135.1.30", {"start": v(-21.65, -12.5) * mm, "end": v(-24.65, -7.3) * mm});
            skLineSegment(sketch, "E135.1.31", {"start": v(-36.75, 7.65) * mm, "end": v(-33.24, 9.68) * mm});
            skLineSegment(sketch, "E135.1.32", {"start": v(-11.75, -35.65) * mm, "end": v(-8.24, -33.62) * mm});
            skLineSegment(sketch, "E135.1.33", {"start": v(-21.65, -12.5) * mm, "end": v(-18.65, -17.7) * mm});
            skArc(sketch, "E135.1.34", {"start": v(-19.52, -3.19) * mm, "mid": v(-18.76, -3.09) * mm, "end": v(-18.16, -3.55) * mm});
            skArc(sketch, "E135.1.35", {"start": v(-37.11, 6.28) * mm, "mid": v(-37.21, 7.04) * mm, "end": v(-36.75, 7.65) * mm});
            skArc(sketch, "E135.1.36", {"start": v(-8.24, -33.62) * mm, "mid": v(-7.79, -33.07) * mm, "end": v(-7.83, -32.35) * mm});
            skArc(sketch, "E135.1.37", {"start": v(-24.65, -7.3) * mm, "mid": v(-24.75, -6.55) * mm, "end": v(-24.28, -5.94) * mm});
            skArc(sketch, "E135.1.38", {"start": v(-18.65, -17.7) * mm, "mid": v(-18.04, -18.16) * mm, "end": v(-17.28, -18.06) * mm});
            skArc(sketch, "E135.1.39", {"start": v(-33.24, 9.68) * mm, "mid": v(-32.53, 9.79) * mm, "end": v(-31.93, 9.4) * mm});
            skArc(sketch, "E135.1.40", {"start": v(-13.11, -35.28) * mm, "mid": v(-12.5, -35.75) * mm, "end": v(-11.75, -35.65) * mm});
            skArc(sketch, "E135.1.41", {"start": v(-12.52, -15.31) * mm, "mid": v(-12.06, -14.7) * mm, "end": v(-12.16, -13.95) * mm});
            skLineSegment(sketch, "E135.2.0", {"start": v(23.38, -13.5) * mm, "end": v(35.88, 8.15) * mm, "construction": true});
            skLineSegment(sketch, "E135.2.1", {"start": v(9.15, -34.15) * mm, "end": v(21.65, -12.5) * mm, "construction": true});
            skCircle(sketch, "E135.2.2", {"center": v(23.23, 0.73) * mm, "radius": 5.25 * mm, "construction": true});
            skCircle(sketch, "E135.2.3", {"center": v(10.98, -20.48) * mm, "radius": 2.1 * mm});
            skPoint(sketch, "E135.2.4", {"position": v(18.66, -2.69) * mm});
            skCircle(sketch, "E135.2.5", {"center": v(10.98, -20.48) * mm, "radius": 5.25 * mm, "construction": true});
            skCircle(sketch, "E135.2.6", {"center": v(35.88, 8.15) * mm, "radius": 2 * mm, "construction": true});
            skLineSegment(sketch, "E135.2.7", {"start": v(25.11, -14.5) * mm, "end": v(13.11, -35.28) * mm});
            skArc(sketch, "E135.2.8", {"start": v(0, -20.3) * mm, "mid": v(7.18, -24.2) * mm, "end": v(7.83, -32.35) * mm});
            skLineSegment(sketch, "E135.2.9", {"start": v(7.42, -33.15) * mm, "end": v(19.92, -11.5) * mm, "construction": true});
            skArc(sketch, "E135.2.10", {"start": v(17.58, 10.15) * mm, "mid": v(24.55, 5.88) * mm, "end": v(31.93, 9.4) * mm});
            skLineSegment(sketch, "E135.2.11", {"start": v(12.16, -13.95) * mm, "end": v(15.16, -8.75) * mm});
            skCircle(sketch, "E135.2.12", {"center": v(23.23, 0.73) * mm, "radius": 2.1 * mm});
            skPoint(sketch, "E135.2.13", {"position": v(7.42, -33.15) * mm});
            skPoint(sketch, "E135.2.14", {"position": v(18.15, -18.56) * mm});
            skLineSegment(sketch, "E135.2.15", {"start": v(0, -20.3) * mm, "end": v(19.46, -20.3) * mm, "construction": true});
            skLineSegment(sketch, "E135.2.16", {"start": v(23.38, -13.5) * mm, "end": v(10.88, -35.15) * mm, "construction": true});
            skCircle(sketch, "E135.2.17", {"center": v(10.88, -35.15) * mm, "radius": 2 * mm, "construction": true});
            skPoint(sketch, "E135.2.18", {"position": v(25.15, -6.44) * mm});
            skLineSegment(sketch, "E135.2.19", {"start": v(32.42, 10.15) * mm, "end": v(19.92, -11.5) * mm, "construction": true});
            skLineSegment(sketch, "E135.2.20", {"start": v(34.15, 9.15) * mm, "end": v(21.65, -12.5) * mm, "construction": true});
            skPoint(sketch, "E135.2.21", {"position": v(11.66, -14.81) * mm});
            skLineSegment(sketch, "E135.2.22", {"start": v(17.28, -18.06) * mm, "end": v(12.52, -15.31) * mm});
            skLineSegment(sketch, "E135.2.23", {"start": v(18.16, -3.55) * mm, "end": v(15.16, -8.75) * mm});
            skPoint(sketch, "E135.2.24", {"position": v(12.61, -36.15) * mm});
            skLineSegment(sketch, "E135.2.25", {"start": v(25.11, -14.5) * mm, "end": v(37.11, 6.28) * mm});
            skPoint(sketch, "E135.2.26", {"position": v(37.61, 7.15) * mm});
            skLineSegment(sketch, "E135.2.27", {"start": v(17.58, 10.15) * mm, "end": v(27.3, -6.7) * mm, "construction": true});
            skPoint(sketch, "E135.2.28", {"position": v(32.42, 10.15) * mm});
            skLineSegment(sketch, "E135.2.29", {"start": v(24.28, -5.94) * mm, "end": v(19.52, -3.19) * mm});
            skLineSegment(sketch, "E135.2.30", {"start": v(21.65, -12.5) * mm, "end": v(18.65, -17.7) * mm});
            skLineSegment(sketch, "E135.2.31", {"start": v(11.75, -35.65) * mm, "end": v(8.24, -33.62) * mm});
            skLineSegment(sketch, "E135.2.32", {"start": v(36.75, 7.65) * mm, "end": v(33.24, 9.68) * mm});
            skLineSegment(sketch, "E135.2.33", {"start": v(21.65, -12.5) * mm, "end": v(24.65, -7.3) * mm});
            skArc(sketch, "E135.2.34", {"start": v(12.52, -15.31) * mm, "mid": v(12.06, -14.7) * mm, "end": v(12.16, -13.95) * mm});
            skArc(sketch, "E135.2.35", {"start": v(13.11, -35.28) * mm, "mid": v(12.5, -35.75) * mm, "end": v(11.75, -35.65) * mm});
            skArc(sketch, "E135.2.36", {"start": v(33.24, 9.68) * mm, "mid": v(32.53, 9.79) * mm, "end": v(31.93, 9.4) * mm});
            skArc(sketch, "E135.2.37", {"start": v(18.65, -17.7) * mm, "mid": v(18.04, -18.16) * mm, "end": v(17.28, -18.06) * mm});
            skArc(sketch, "E135.2.38", {"start": v(24.65, -7.3) * mm, "mid": v(24.75, -6.55) * mm, "end": v(24.28, -5.94) * mm});
            skArc(sketch, "E135.2.39", {"start": v(8.24, -33.62) * mm, "mid": v(7.79, -33.07) * mm, "end": v(7.83, -32.35) * mm});
            skArc(sketch, "E135.2.40", {"start": v(37.11, 6.28) * mm, "mid": v(37.21, 7.04) * mm, "end": v(36.75, 7.65) * mm});
            skArc(sketch, "E135.2.41", {"start": v(19.52, -3.19) * mm, "mid": v(18.76, -3.09) * mm, "end": v(18.16, -3.55) * mm});
            skSolve(sketch);
        }
        {
            var Q0;
            Q0 = qSketchRegion(id + "F4", true);
            extrude(context, id + "F5", {"entities" : qUnion([Q0]), "oppositeDirection" : true, "depth" : 2 * mm, "offsetDistance" : 25 * mm});
        }
    });
